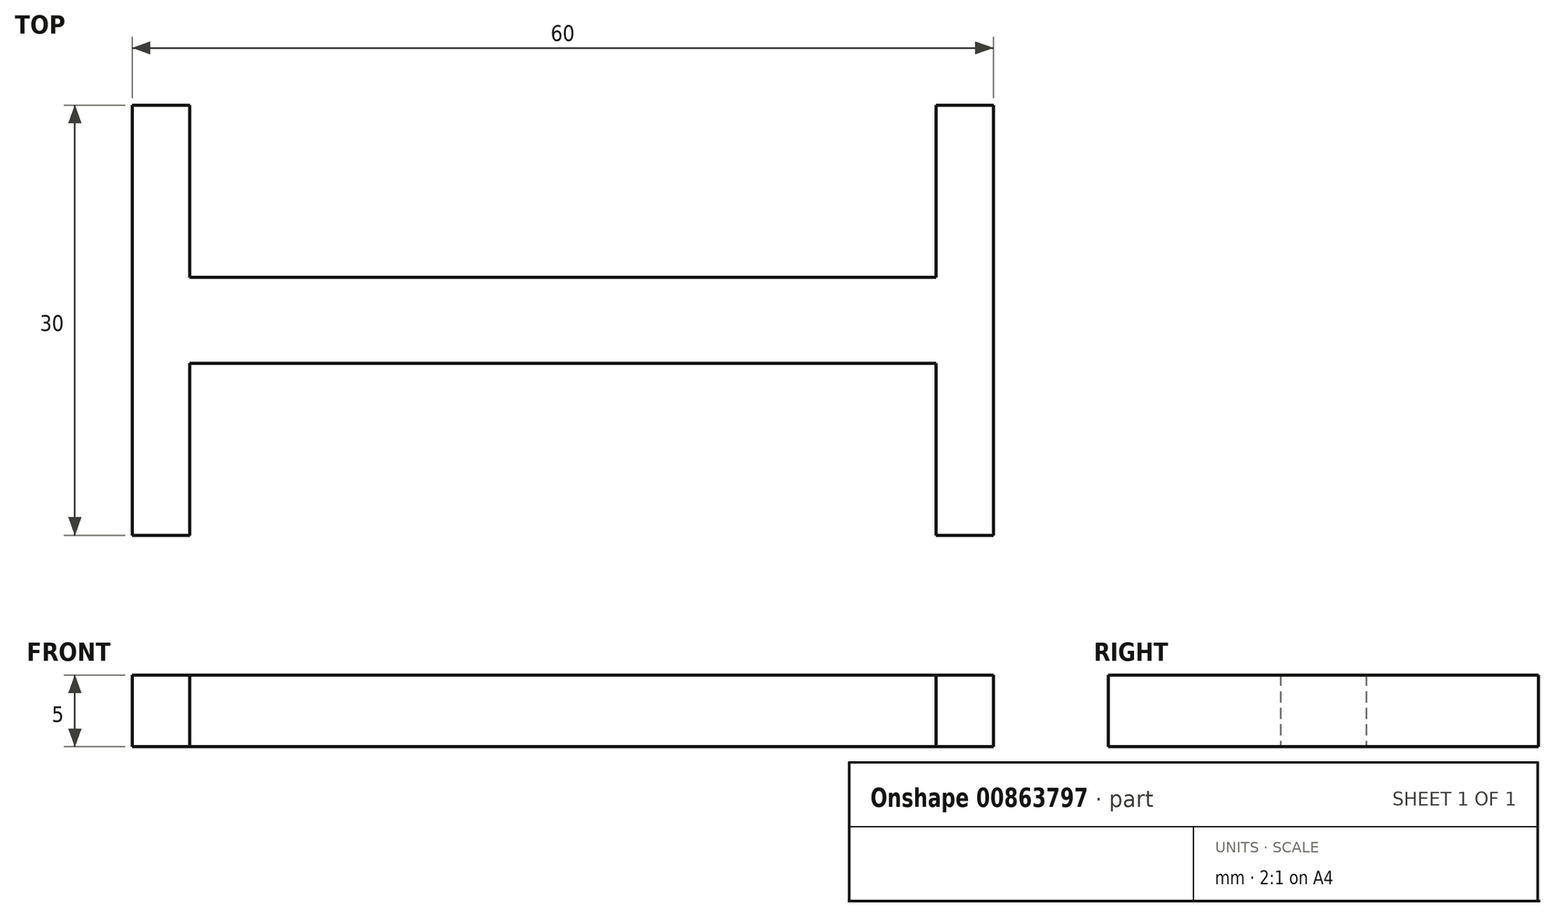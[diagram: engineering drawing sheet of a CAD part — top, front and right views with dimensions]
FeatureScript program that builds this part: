
annotation { "Feature Type Name" : "Feature", "Feature Type Description" : "" }
export const myFeature = defineFeature(function(context is Context, id is Id, definition is map)
    precondition{}
    {
        {
            var Q0;
            Q0=qCreatedBy(makeId("Top.planeOp"),FACE);
            var sketch = newSketch(context, id + "F0", { "sketchPlane" : qUnion([Q0])});
            skLineSegment(sketch, "E0.bottom", {"start": v(30, 3) * mm, "end": v(-30, 3) * mm});
            skLineSegment(sketch, "E0.top", {"start": v(30, -3) * mm, "end": v(-30, -3) * mm});
            skLineSegment(sketch, "E0.left", {"start": v(30, 3) * mm, "end": v(30, -3) * mm});
            skLineSegment(sketch, "E0.right", {"start": v(-30, 3) * mm, "end": v(-30, -3) * mm});
            skPoint(sketch, "E0.middle", {"position": v(0, 0) * mm});
            skLineSegment(sketch, "E1.bottom", {"start": v(-26, 15) * mm, "end": v(-30, 15) * mm});
            skLineSegment(sketch, "E1.top", {"start": v(-26, -15) * mm, "end": v(-30, -15) * mm});
            skLineSegment(sketch, "E1.left", {"start": v(-26, 15) * mm, "end": v(-26, -15) * mm});
            skLineSegment(sketch, "E1.right", {"start": v(-30, 15) * mm, "end": v(-30, -15) * mm});
            skPoint(sketch, "E1.middle", {"position": v(-28, 0) * mm});
            skPoint(sketch, "E1.middle.positionSnap0", {"position": v(-30, 0) * mm});
            skPoint(sketch, "E1.centerSnap0", {"position": v(-30, 0) * mm});
            skLineSegment(sketch, "E2.bottom", {"start": v(30, 15) * mm, "end": v(26, 15) * mm});
            skLineSegment(sketch, "E2.top", {"start": v(30, -15) * mm, "end": v(26, -15) * mm});
            skLineSegment(sketch, "E2.left", {"start": v(30, 15) * mm, "end": v(30, -15) * mm});
            skLineSegment(sketch, "E2.right", {"start": v(26, 15) * mm, "end": v(26, -15) * mm});
            skPoint(sketch, "E2.middle", {"position": v(28, 0) * mm});
            skPoint(sketch, "E2.middle.positionSnap0", {"position": v(30, 0) * mm});
            skPoint(sketch, "E2.centerSnap0", {"position": v(30, 0) * mm});
            skSolve(sketch);
        }
        {
            var Q0;
            Q0 = qSketchRegion(id + "F0", true);
            extrude(context, id + "F1", {"entities" : qUnion([Q0]), "depth" : 5 * mm, "offsetDistance" : 25 * mm});
        }
    });
